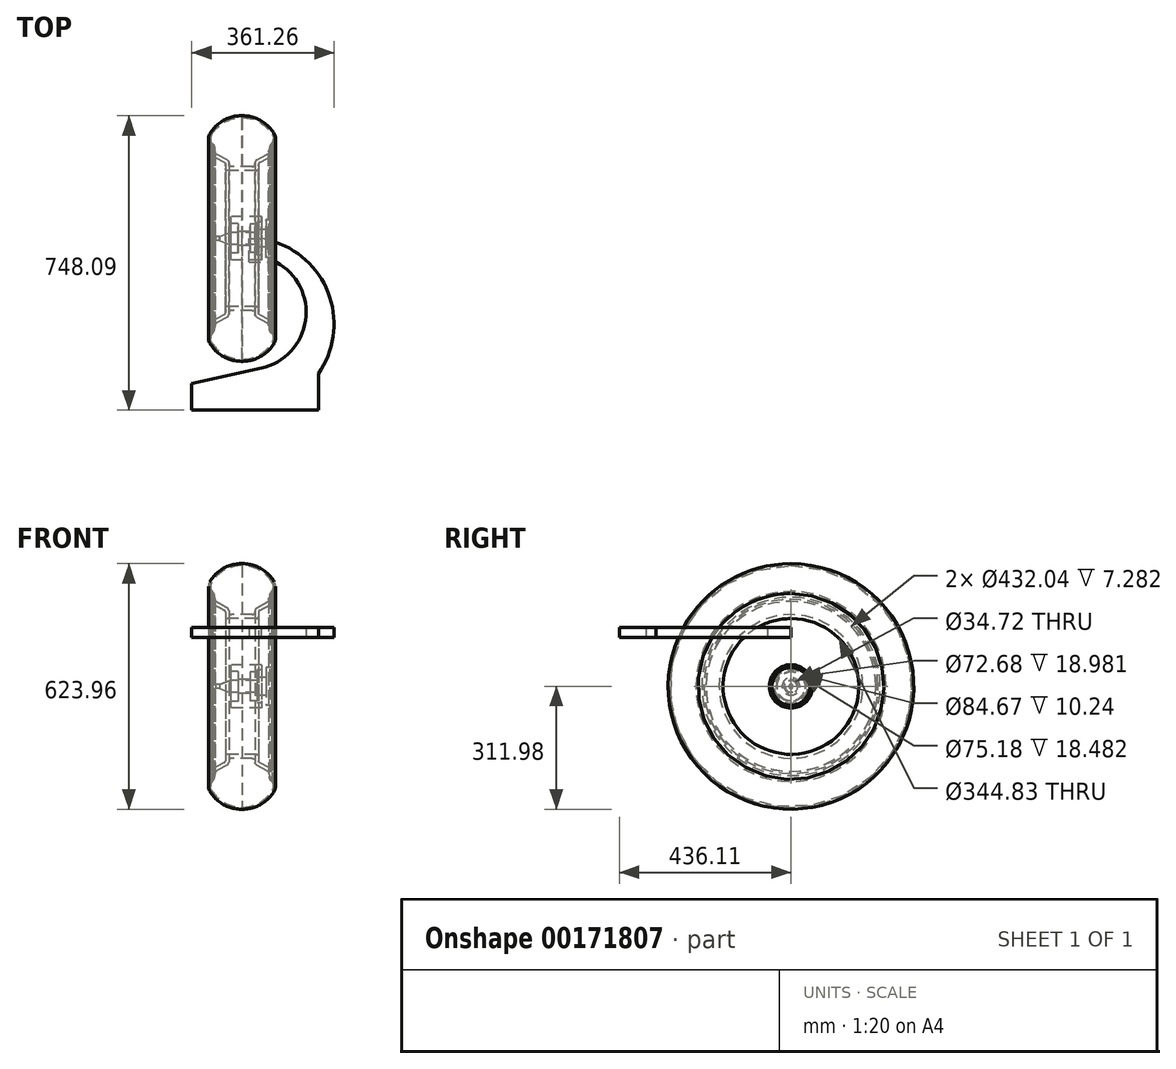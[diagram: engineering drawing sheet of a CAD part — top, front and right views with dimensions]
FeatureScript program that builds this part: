
annotation { "Feature Type Name" : "Feature", "Feature Type Description" : "" }
export const myFeature = defineFeature(function(context is Context, id is Id, definition is map)
    precondition{}
    {
        {
            var Q0;
            Q0=qCreatedBy(makeId("Front.planeOp"),FACE);
            var sketch = newSketch(context, id + "F0", { "sketchPlane" : qUnion([Q0])});
            skLineSegment(sketch, "E0", {"start": v(-97.42, 0) * mm, "end": v(103.93, 0) * mm, "construction": true});
            skLineSegment(sketch, "E1", {"start": v(0, 0) * mm, "end": v(0, 307.94) * mm, "construction": true});
            skLineSegment(sketch, "E2", {"start": v(-79.1, 211.13) * mm, "end": v(-79.1, 230.67) * mm});
            skLineSegment(sketch, "E3", {"start": v(-75, 230.9) * mm, "end": v(-75, 215.9) * mm});
            skLineSegment(sketch, "E4", {"start": v(-75, 215.9) * mm, "end": v(-71.65, 215.9) * mm});
            skLineSegment(sketch, "E5", {"start": v(-37.2, 199.15) * mm, "end": v(-62.64, 213.53) * mm});
            skLineSegment(sketch, "E6", {"start": v(-41.73, 177.2) * mm, "end": v(-41.73, 188.7) * mm});
            skLineSegment(sketch, "E7", {"start": v(-44.3, 192.95) * mm, "end": v(-65.75, 204.12) * mm});
            skLineSegment(sketch, "E8", {"start": v(-70.28, 205.63) * mm, "end": v(-75.09, 206.42) * mm});
            skArc(sketch, "E9", {"start": v(-79.1, 230.67) * mm, "mid": v(-79.77, 232.64) * mm, "end": v(-81.51, 233.78) * mm});
            skArc(sketch, "E10", {"start": v(-81.51, 235.98) * mm, "mid": v(-82.37, 234.88) * mm, "end": v(-81.51, 233.78) * mm});
            skArc(sketch, "E11", {"start": v(-75, 230.9) * mm, "mid": v(-77.02, 235.03) * mm, "end": v(-81.51, 235.98) * mm});
            skPoint(sketch, "E12.visualSharp", {"position": v(-79.1, 207.07) * mm});
            skArc(sketch, "E12.filletArc", {"start": v(-79.1, 211.13) * mm, "mid": v(-77.95, 208.04) * mm, "end": v(-75.09, 206.42) * mm});
            skPoint(sketch, "E13.visualSharp", {"position": v(-66.83, 215.9) * mm});
            skArc(sketch, "E13.filletArc", {"start": v(-62.64, 213.53) * mm, "mid": v(-67, 215.3) * mm, "end": v(-71.65, 215.9) * mm});
            skPoint(sketch, "E14.visualSharp", {"position": v(-67.9, 205.24) * mm});
            skArc(sketch, "E14.filletArc", {"start": v(-65.75, 204.12) * mm, "mid": v(-67.95, 205.06) * mm, "end": v(-70.28, 205.63) * mm});
            skPoint(sketch, "E15.visualSharp", {"position": v(-41.73, 191.6) * mm});
            skArc(sketch, "E15.filletArc", {"start": v(-41.73, 188.7) * mm, "mid": v(-42.43, 191.19) * mm, "end": v(-44.3, 192.95) * mm});
            skPoint(sketch, "E16.visualSharp", {"position": v(-41.73, 172.41) * mm});
            skArc(sketch, "E16.filletArc", {"start": v(-41.73, 177.2) * mm, "mid": v(-40.33, 173.81) * mm, "end": v(-36.96, 172.41) * mm});
            skPoint(sketch, "E17.visualSharp", {"position": v(-32.3, 196.38) * mm});
            skLineSegment(sketch, "E18", {"start": v(0, 172.41) * mm, "end": v(-36.96, 172.41) * mm});
            skLineSegment(sketch, "E19", {"start": v(-33.4, 192.64) * mm, "end": v(-33.4, 190.09) * mm});
            skLineSegment(sketch, "E20", {"start": v(-25.92, 182.6) * mm, "end": v(0, 182.6) * mm});
            skPoint(sketch, "E21.visualSharp", {"position": v(-33.4, 197) * mm});
            skArc(sketch, "E21.filletArc", {"start": v(-33.4, 192.64) * mm, "mid": v(-34.42, 196.4) * mm, "end": v(-37.2, 199.15) * mm});
            skPoint(sketch, "E22.visualSharp", {"position": v(-33.4, 182.6) * mm});
            skArc(sketch, "E22.filletArc", {"start": v(-33.4, 190.09) * mm, "mid": v(-31.2, 184.8) * mm, "end": v(-25.92, 182.6) * mm});
            skArc(sketch, "E23.MirrorCS", {"start": v(81.51, 235.98) * mm, "mid": v(82.37, 234.88) * mm, "end": v(81.51, 233.78) * mm});
            skArc(sketch, "E24.MirrorCS", {"start": v(79.1, 230.67) * mm, "mid": v(79.77, 232.64) * mm, "end": v(81.51, 233.78) * mm});
            skLineSegment(sketch, "E25.MirrorCS", {"start": v(75, 215.9) * mm, "end": v(71.65, 215.9) * mm});
            skLineSegment(sketch, "E26.MirrorCS", {"start": v(33.4, 192.64) * mm, "end": v(33.4, 190.09) * mm});
            skArc(sketch, "E27.MirrorCS", {"start": v(33.4, 192.64) * mm, "mid": v(34.42, 196.4) * mm, "end": v(37.2, 199.15) * mm});
            skArc(sketch, "E28.MirrorCS", {"start": v(79.1, 211.13) * mm, "mid": v(77.95, 208.04) * mm, "end": v(75.09, 206.42) * mm});
            skArc(sketch, "E29.MirrorCS", {"start": v(41.73, 188.7) * mm, "mid": v(42.43, 191.19) * mm, "end": v(44.3, 192.95) * mm});
            skArc(sketch, "E30.MirrorCS", {"start": v(65.75, 204.12) * mm, "mid": v(67.95, 205.06) * mm, "end": v(70.28, 205.63) * mm});
            skLineSegment(sketch, "E31.MirrorCS", {"start": v(79.1, 211.13) * mm, "end": v(79.1, 230.67) * mm});
            skArc(sketch, "E32.MirrorCS", {"start": v(75, 230.9) * mm, "mid": v(77.02, 235.03) * mm, "end": v(81.51, 235.98) * mm});
            skLineSegment(sketch, "E33.MirrorCS", {"start": v(70.28, 205.63) * mm, "end": v(75.09, 206.42) * mm});
            skLineSegment(sketch, "E34.MirrorCS", {"start": v(75, 230.9) * mm, "end": v(75, 215.9) * mm});
            skPoint(sketch, "E35.MirrorP", {"position": v(79.1, 207.07) * mm});
            skArc(sketch, "E36.MirrorCS", {"start": v(33.4, 190.09) * mm, "mid": v(31.2, 184.8) * mm, "end": v(25.92, 182.6) * mm});
            skLineSegment(sketch, "E37.MirrorCS", {"start": v(41.73, 177.2) * mm, "end": v(41.73, 188.7) * mm});
            skPoint(sketch, "E38.MirrorP", {"position": v(41.73, 172.41) * mm});
            skArc(sketch, "E39.MirrorCS", {"start": v(62.64, 213.53) * mm, "mid": v(67, 215.3) * mm, "end": v(71.65, 215.9) * mm});
            skArc(sketch, "E40.MirrorCS", {"start": v(41.73, 177.2) * mm, "mid": v(40.33, 173.81) * mm, "end": v(36.96, 172.41) * mm});
            skLineSegment(sketch, "E41.MirrorCS", {"start": v(0, 172.41) * mm, "end": v(36.96, 172.41) * mm});
            skPoint(sketch, "E42.MirrorP", {"position": v(41.73, 191.6) * mm});
            skLineSegment(sketch, "E43.MirrorCS", {"start": v(37.2, 199.15) * mm, "end": v(62.64, 213.53) * mm});
            skPoint(sketch, "E44.MirrorP", {"position": v(33.4, 182.6) * mm});
            skPoint(sketch, "E45.MirrorP", {"position": v(33.4, 197) * mm});
            skPoint(sketch, "E46.MirrorP", {"position": v(66.83, 215.9) * mm});
            skPoint(sketch, "E47.MirrorP", {"position": v(32.3, 196.38) * mm});
            skPoint(sketch, "E48.MirrorP", {"position": v(67.9, 205.24) * mm});
            skLineSegment(sketch, "E49.MirrorCS", {"start": v(25.92, 182.6) * mm, "end": v(0, 182.6) * mm});
            skLineSegment(sketch, "E50.MirrorCS", {"start": v(44.3, 192.95) * mm, "end": v(65.75, 204.12) * mm});
            skSolve(sketch);
        }
        {
            var Q0;
            Q0 = qSketchRegion(id + "F0", true);
            var Q1;
            Q1=sQuery(id+"F0.wireOp",EDGE,"E0");
            revolve(context, id + "F1", {"entities" : qUnion([Q0]), "axis" : qUnion([Q1]), "revolveType" : RevolveType.FULL});
        }
        {
            var Q0;
            Q0=qCreatedBy(makeId("Front.planeOp"),FACE);
            var sketch = newSketch(context, id + "F2", { "sketchPlane" : qUnion([Q0])});
            skLineSegment(sketch, "E51", {"start": v(-75, 216.02) * mm, "end": v(-75, 229.82) * mm});
            skArc(sketch, "E52", {"start": v(-75, 229.82) * mm, "mid": v(-75.74, 233.37) * mm, "end": v(-77.82, 236.34) * mm});
            skLineSegment(sketch, "E53", {"start": v(-75, 216.02) * mm, "end": v(-67.72, 216.02) * mm});
            skLineSegment(sketch, "E54", {"start": v(-67.72, 216.02) * mm, "end": v(-67.72, 221.32) * mm});
            skLineSegment(sketch, "E55", {"start": v(-67.72, 221.32) * mm, "end": v(-69.58, 226.58) * mm});
            skArc(sketch, "E56", {"start": v(-82.13, 265.37) * mm, "mid": v(-85.03, 250.1) * mm, "end": v(-77.82, 236.34) * mm});
            skArc(sketch, "E57.2", {"start": v(-69.58, 226.58) * mm, "mid": v(-70.9, 234.84) * mm, "end": v(-75.88, 241.54) * mm});
            skLineSegment(sketch, "E58", {"start": v(0, 0) * mm, "end": v(0, 505.4) * mm, "construction": true});
            skLineSegment(sketch, "E59", {"start": v(-1.46, 311.98) * mm, "end": v(1.46, 311.98) * mm});
            skArc(sketch, "E60", {"start": v(-1.46, 311.98) * mm, "mid": v(-48.04, 299.49) * mm, "end": v(-82.13, 265.37) * mm});
            skArc(sketch, "E61.0", {"start": v(-77.8, 262.87) * mm, "mid": v(-80.21, 251.9) * mm, "end": v(-75.88, 241.54) * mm});
            skArc(sketch, "E61.1", {"start": v(0, 306.97) * mm, "mid": v(-44.9, 295.52) * mm, "end": v(-77.8, 262.87) * mm});
            skLineSegment(sketch, "E62", {"start": v(0, 306.97) * mm, "end": v(0, 306.97) * mm});
            skLineSegment(sketch, "E63.MirrorCS", {"start": v(67.72, 216.02) * mm, "end": v(67.72, 221.32) * mm});
            skArc(sketch, "E64.MirrorCS", {"start": v(1.46, 311.98) * mm, "mid": v(48.04, 299.49) * mm, "end": v(82.13, 265.37) * mm});
            skArc(sketch, "E65.MirrorCS", {"start": v(69.58, 226.58) * mm, "mid": v(70.9, 234.84) * mm, "end": v(75.88, 241.54) * mm});
            skLineSegment(sketch, "E66.MirrorCS", {"start": v(75, 216.02) * mm, "end": v(75, 229.82) * mm});
            skLineSegment(sketch, "E67.MirrorCS", {"start": v(75, 216.02) * mm, "end": v(67.72, 216.02) * mm});
            skLineSegment(sketch, "E68.MirrorCS", {"start": v(67.72, 221.32) * mm, "end": v(69.58, 226.58) * mm});
            skArc(sketch, "E69.MirrorCS", {"start": v(0, 306.97) * mm, "mid": v(44.9, 295.52) * mm, "end": v(77.8, 262.87) * mm});
            skArc(sketch, "E70.MirrorCS", {"start": v(77.8, 262.87) * mm, "mid": v(80.21, 251.9) * mm, "end": v(75.88, 241.54) * mm});
            skArc(sketch, "E71.MirrorCS", {"start": v(75, 229.82) * mm, "mid": v(75.74, 233.37) * mm, "end": v(77.82, 236.34) * mm});
            skArc(sketch, "E72.MirrorCS", {"start": v(82.13, 265.37) * mm, "mid": v(85.03, 250.1) * mm, "end": v(77.82, 236.34) * mm});
            skLineSegment(sketch, "E73", {"start": v(-195.27, 0) * mm, "end": v(154.3, 0) * mm, "construction": true});
            skSolve(sketch);
        }
        {
            var Q0;
            Q0 = qSketchRegion(id + "F2", true);
            var Q1;
            Q1=sQuery(id+"F2.wireOp",EDGE,"E73");
            revolve(context, id + "F3", {"entities" : qUnion([Q0]), "axis" : qUnion([Q1]), "revolveType" : RevolveType.FULL});
        }
        {
            var Q0;
            Q0=qCreatedBy(makeId("Front.planeOp"),FACE);
            var sketch = newSketch(context, id + "F4", { "sketchPlane" : qUnion([Q0])});
            skLineSegment(sketch, "E74", {"start": v(-90.73, 0) * mm, "end": v(89.02, 0) * mm, "construction": true});
            skLineSegment(sketch, "E75", {"start": v(74.63, 0) * mm, "end": v(74.63, 48.06) * mm});
            skLineSegment(sketch, "E76", {"start": v(74.63, 48.06) * mm, "end": v(60.62, 48.06) * mm});
            skLineSegment(sketch, "E77", {"start": v(60.62, 48.06) * mm, "end": v(60.62, 22.38) * mm});
            skLineSegment(sketch, "E78", {"start": v(60.62, 22.38) * mm, "end": v(38.48, 22.38) * mm});
            skLineSegment(sketch, "E79", {"start": v(38.48, 22.38) * mm, "end": v(38.48, 14.95) * mm});
            skLineSegment(sketch, "E80", {"start": v(38.48, 14.95) * mm, "end": v(0, 14.95) * mm});
            skLineSegment(sketch, "E81", {"start": v(0, 14.95) * mm, "end": v(-31.97, 14.95) * mm});
            skLineSegment(sketch, "E82", {"start": v(-31.97, 14.95) * mm, "end": v(-57.26, 5.22) * mm});
            skLineSegment(sketch, "E83", {"start": v(-57.26, 5.22) * mm, "end": v(-67.64, 5.22) * mm});
            skLineSegment(sketch, "E84", {"start": v(-67.64, 5.22) * mm, "end": v(-67.64, 0) * mm});
            skLineSegment(sketch, "E85", {"start": v(-67.64, 0) * mm, "end": v(74.63, 0) * mm});
            skSolve(sketch);
        }
        {
            var Q0;
            Q0 = qSketchRegion(id + "F4", true);
            var Q1;
            Q1=sQuery(id+"F4.wireOp",EDGE,"E74");
            revolve(context, id + "F5", {"entities" : qUnion([Q0]), "axis" : qUnion([Q1]), "revolveType" : RevolveType.FULL});
        }
        {
            var Q0;
            Q0=qCreatedBy(makeId("Front.planeOp"),FACE);
            var sketch = newSketch(context, id + "F6", { "sketchPlane" : qUnion([Q0])});
            skLineSegment(sketch, "E86", {"start": v(-76.35, 0) * mm, "end": v(75.3, 0) * mm, "construction": true});
            skPoint(sketch, "E87", {"position": v(0, 72.71) * mm});
            skSolve(sketch);
        }
        {
            var Q0;
            Q0=sQuery(id+"F6.wireOp",EDGE,"E86");
            var Q1;
            Q1=sQuery(id+"F6.wireOp",VERTEX,"E87");
            cPlane(context, id + "F7", {"entities" : qUnion([Q0, Q1]), "cplaneType" : CPlaneType.LINE_ANGLE, "offset" : 25 * mm, "angle" : 10 * degree, "width" : 150 * mm, "height" : 150 * mm});
        }
        {
            var Q0;
            Q0=qCreatedBy(id+"F7.planeOp",FACE);
            var sketch = newSketch(context, id + "F8", { "sketchPlane" : qUnion([Q0])});
            skLineSegment(sketch, "E88", {"start": v(0, 17.36) * mm, "end": v(19.96, 17.36) * mm});
            skLineSegment(sketch, "E89", {"start": v(19.96, 17.36) * mm, "end": v(19.96, 36.34) * mm});
            skLineSegment(sketch, "E90", {"start": v(19.96, 36.34) * mm, "end": v(38.94, 36.34) * mm});
            skLineSegment(sketch, "E91", {"start": v(38.94, 36.34) * mm, "end": v(38.94, 42.33) * mm});
            skLineSegment(sketch, "E92", {"start": v(38.94, 42.33) * mm, "end": v(49.18, 42.33) * mm});
            skLineSegment(sketch, "E93", {"start": v(49.18, 42.33) * mm, "end": v(49.18, 55.07) * mm});
            skLineSegment(sketch, "E94", {"start": v(0, 17.36) * mm, "end": v(-10.26, 17.36) * mm});
            skLineSegment(sketch, "E95", {"start": v(-10.26, 17.36) * mm, "end": v(-10.26, 37.59) * mm});
            skLineSegment(sketch, "E96", {"start": v(-10.26, 37.59) * mm, "end": v(-28.74, 37.59) * mm});
            skLineSegment(sketch, "E97", {"start": v(-28.74, 37.59) * mm, "end": v(-28.74, 55.07) * mm});
            skLineSegment(sketch, "E98", {"start": v(-28.74, 55.07) * mm, "end": v(49.18, 55.07) * mm});
            skLineSegment(sketch, "E99", {"start": v(-76.7, 0) * mm, "end": v(81.9, 0) * mm, "construction": true});
            skSolve(sketch);
        }
        {
            var Q0;
            Q0 = qSketchRegion(id + "F8", true);
            var Q1;
            Q1=sQuery(id+"F8.wireOp",EDGE,"E99");
            revolve(context, id + "F9", {"entities" : qUnion([Q0]), "axis" : qUnion([Q1]), "revolveType" : RevolveType.FULL});
        }
        {
            var Q0;
            Q0=qCreatedBy(makeId("Top.planeOp"),FACE);
            cPlane(context, id + "F10", {"entities" : qUnion([Q0]), "cplaneType" : CPlaneType.OFFSET, "offset" : 125 * mm, "width" : 150 * mm, "height" : 150 * mm});
        }
        {
            var Q0;
            Q0=qCreatedBy(id+"F10.planeOp",FACE);
            var sketch = newSketch(context, id + "F11", { "sketchPlane" : qUnion([Q0])});
            skLineSegment(sketch, "E100", {"start": v(17.61, -60.03) * mm, "end": v(87.13, -60.03) * mm});
            skArc(sketch, "E101", {"start": v(49.2, -329.45) * mm, "mid": v(161.63, -207.9) * mm, "end": v(87.13, -60.03) * mm});
            skLineSegment(sketch, "E102", {"start": v(49.2, -329.45) * mm, "end": v(-127.4, -368.52) * mm});
            skLineSegment(sketch, "E103", {"start": v(-127.4, -368.52) * mm, "end": v(-127.4, -436.11) * mm});
            skLineSegment(sketch, "E104", {"start": v(-127.4, -436.11) * mm, "end": v(194.19, -436.11) * mm});
            skLineSegment(sketch, "E105", {"start": v(194.19, -436.11) * mm, "end": v(194.19, -343.28) * mm});
            skLineSegment(sketch, "E106", {"start": v(17.61, -60.03) * mm, "end": v(17.61, 0) * mm});
            skLineSegment(sketch, "E107", {"start": v(17.61, 0) * mm, "end": v(47.94, 0) * mm});
            skArc(sketch, "E108", {"start": v(194.19, -343.28) * mm, "mid": v(216.27, -131.08) * mm, "end": v(47.94, 0) * mm});
            skSolve(sketch);
        }
        {
            var Q0;
            Q0 = qSketchRegion(id + "F11", true);
            extrude(context, id + "F12", {"entities" : qUnion([Q0]), "depth" : 25 * mm});
        }
    });
